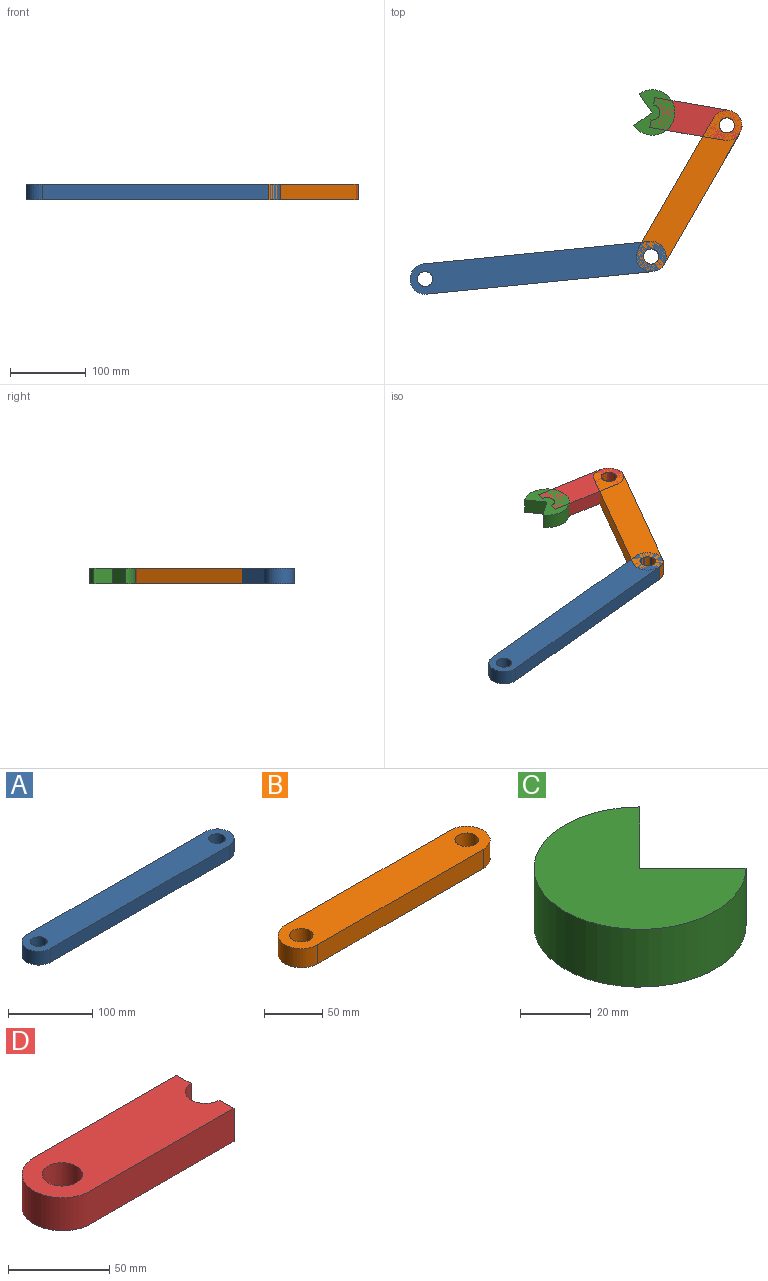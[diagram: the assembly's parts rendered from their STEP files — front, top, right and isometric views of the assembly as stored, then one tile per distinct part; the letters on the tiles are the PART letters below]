
ASSEMBLY  parts=4 mates=3
PART A: 8 faces, bbox 340x40x20 mm
  f0: plane 300x20mm, normal (0,1,0), area 6000mm2, adj f1,f3,f6,f7
  f1: cylinder r=20mm len=40mm, axis (0,0,-1), area 1256.6mm2, adj f0,f2,f6,f7
  f2: plane 300x20mm, normal (0,-1,0), area 6000mm2, adj f1,f3,f6,f7
  f3: cylinder r=20mm len=40mm, axis (0,0,-1), area 1256.6mm2, adj f0,f2,f6,f7
  f4: cylinder r=10mm len=20mm, axis (0,0,-1), area 1256.6mm2, adj f6,f7
  f5: cylinder r=10mm len=20mm, axis (0,0,-1), area 1256.6mm2, adj f6,f7
  f6: plane 340x40mm, normal (0,0,1), area 12628.3mm2, adj f0,f1,f2,f3,f4,f5
  f7: plane 340x40mm, normal (0,0,-1), area 12628.3mm2, adj f0,f1,f2,f3,f4,f5
PART B: 8 faces, bbox 240x40x20 mm
  f0: plane 200x20mm, normal (0,1,0), area 4000mm2, adj f1,f3,f6,f7
  f1: cylinder r=20mm len=40mm, axis (0,0,-1), area 1256.6mm2, adj f0,f2,f6,f7
  f2: plane 200x20mm, normal (0,-1,0), area 4000mm2, adj f1,f3,f6,f7
  f3: cylinder r=20mm len=40mm, axis (0,0,-1), area 1256.6mm2, adj f0,f2,f6,f7
  f4: cylinder r=10mm len=20mm, axis (0,0,-1), area 1256.6mm2, adj f6,f7
  f5: cylinder r=10mm len=20mm, axis (0,0,-1), area 1256.6mm2, adj f6,f7
  f6: plane 240x40mm, normal (0,0,1), area 8628.3mm2, adj f0,f1,f2,f3,f4,f5
  f7: plane 240x40mm, normal (0,0,-1), area 8628.3mm2, adj f0,f1,f2,f3,f4,f5
PART C: 5 faces, bbox 51.2x60x20 mm
  f0: plane 21.21x21.21mm, normal (0.71,0.71,0), area 600mm2, adj f1,f2,f3,f4
  f1: plane 21.21x21.21mm, normal (0.71,-0.71,0), area 600mm2, adj f0,f2,f3,f4
  f2: cylinder r=30mm len=60mm, axis (0,0,-1), area 2827.4mm2, adj f0,f1,f3,f4
  f3: plane 60x51.21mm, normal (0,0,1), area 2120.6mm2, adj f0,f1,f2
  f4: plane 60x51.21mm, normal (0,0,-1), area 2120.6mm2, adj f0,f1,f2
PART D: 9 faces, bbox 120x40x20 mm
  f0: cylinder r=10mm len=20mm, axis (0,0,-1), area 628.3mm2, adj f1,f5,f7,f8
  f1: plane 20x10mm, normal (1,0,0), area 200mm2, adj f0,f2,f7,f8
  f2: plane 100x20mm, normal (0,1,0), area 2000mm2, adj f1,f3,f7,f8
  f3: cylinder r=20mm len=40mm, axis (0,0,-1), area 1256.6mm2, adj f2,f4,f7,f8
  f4: plane 100x20mm, normal (0,-1,0), area 2000mm2, adj f3,f5,f7,f8
  f5: plane 20x10mm, normal (1,0,0), area 200mm2, adj f0,f4,f7,f8
  f6: cylinder r=10mm len=20mm, axis (0,0,-1), area 1256.6mm2, adj f7,f8
  f7: plane 120x40mm, normal (0,0,1), area 4157.1mm2, adj f0,f1,f2,f3,f4,f5,f6
  f8: plane 120x40mm, normal (0,0,-1), area 4157.1mm2, adj f0,f1,f2,f3,f4,f5,f6
PLACE A rot(axis=(0,0,1),5.7deg) t=(0,0,-10)mm
PLACE B rot(axis=(0,0,1),60deg) t=(298.52,29.75,-10)mm
PLACE C rot(axis=(0,0,1),170.2deg) t=(300,220,-10)mm
PLACE D rot(axis=(0,0,1),170.2deg) t=(398.54,202.95,-10)mm
MATE revolute B.f5 <-> A.f4  axis (0,0,-1) through (298.52,29.75,0)mm
MATE revolute D.f6 <-> B.f4  axis (0,0,-1) through (398.54,202.95,0)mm
MATE fastened C.f2 <-> D.f0  axis (0,0,-1) through (300,220,0)mm
